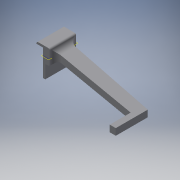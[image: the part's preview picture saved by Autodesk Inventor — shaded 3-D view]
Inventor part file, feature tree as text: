
AUTODESK INVENTOR PART (.ipt)
format: ipt  version: 2018 (Build 220112000, 112)  size: 151,040 bytes
history: native  units: in
note: dims shown in document units (in); Inventor stores cm internally (conversion verified against a paired STEP export)
features: sketch x9, other x3, plane x1
ambient origin geometry x8: Origin, YZ Plane, XZ Plane, XY Plane, X Axis, Y Axis, Z Axis, Center Point
bodies: Solid1 (feature_tree)
feature tree (13):
  other  "AngleArm.ipt"
  other  "Solid1::AngleArm.ipt"
  other  "TaggingFeature1"
  sketch  "Sketch1"  dims[d0=0.3937in]
  sketch  "Sketch2"
  sketch  "Sketch4"
  sketch  "Sketch5"
  sketch  "Sketch6"
  sketch  "Sketch7"
  sketch  "Sketch8"
  sketch  "Sketch9"
  sketch  "Sketch11"
  plane  "Work Plane1"
